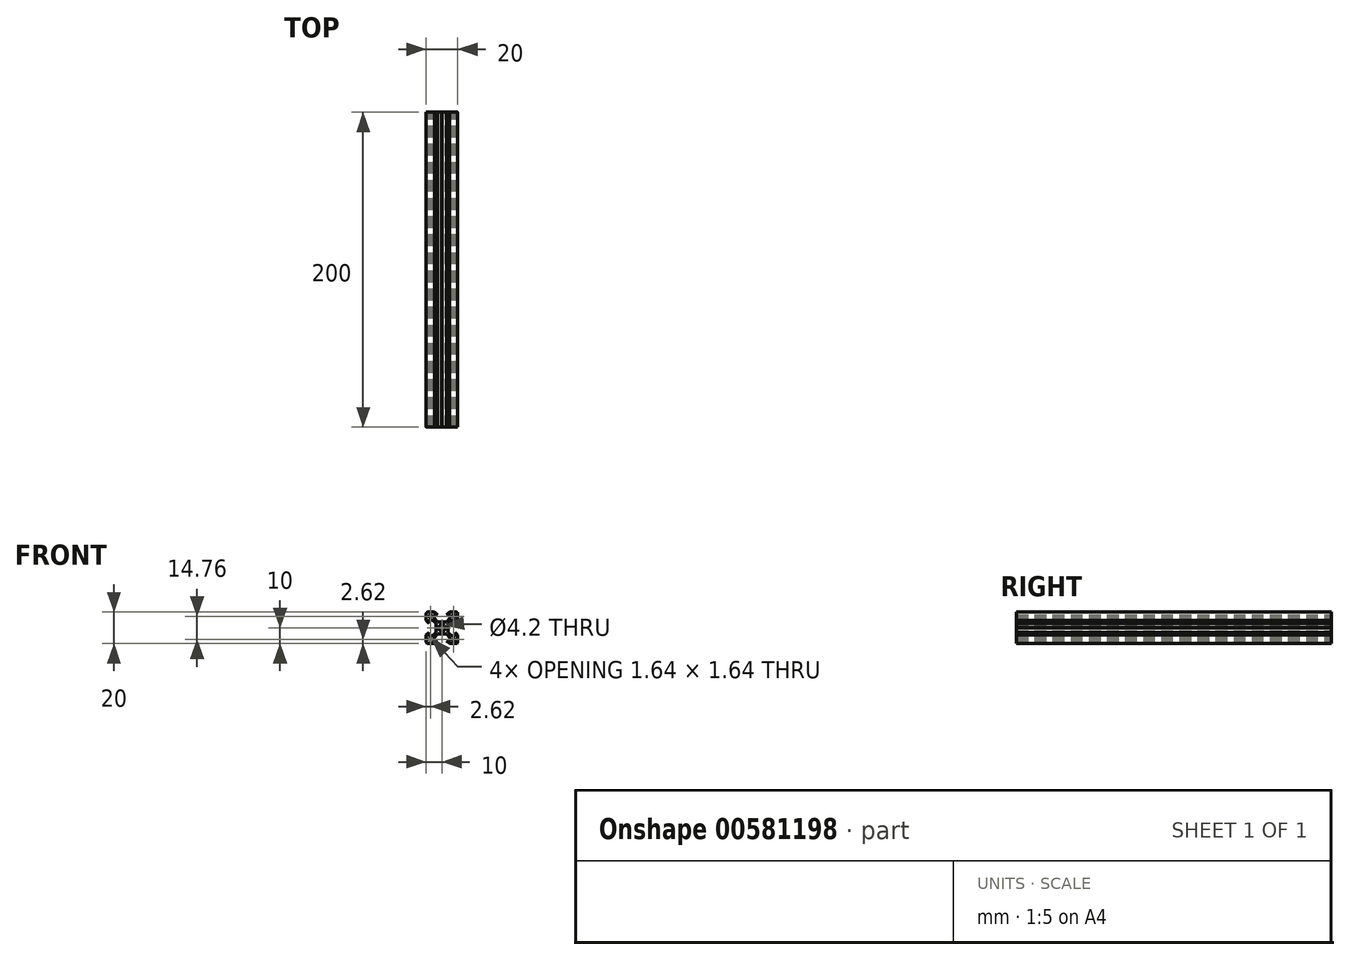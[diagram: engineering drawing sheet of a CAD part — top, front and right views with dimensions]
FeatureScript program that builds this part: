
annotation { "Feature Type Name" : "Feature", "Feature Type Description" : "" }
export const myFeature = defineFeature(function(context is Context, id is Id, definition is map)
    precondition{}
    {
        {
            var Q0;
            Q0=qCreatedBy(makeId("Front.planeOp"),FACE);
            var sketch = newSketch(context, id + "F0", { "sketchPlane" : qUnion([Q0])});
            skLineSegment(sketch, "E0.rect.bottom", {"start": v(-9, 10) * mm, "end": v(9, 10) * mm});
            skLineSegment(sketch, "E0.rect.top", {"start": v(-9, -10) * mm, "end": v(9, -10) * mm});
            skLineSegment(sketch, "E0.rect.left", {"start": v(-10, 9) * mm, "end": v(-10, -9) * mm});
            skLineSegment(sketch, "E0.rect.right", {"start": v(10, 9) * mm, "end": v(10, -9) * mm});
            skPoint(sketch, "E0.rect.middle", {"position": v(0, 0) * mm});
            skCircle(sketch, "E1", {"center": v(0, 0) * mm, "radius": 2.1 * mm});
            skPoint(sketch, "E2.visualSharp", {"position": v(-10, 10) * mm});
            skArc(sketch, "E2.filletArc", {"start": v(-9, 10) * mm, "mid": v(-9.7, 9.7) * mm, "end": v(-10, 9) * mm});
            skPoint(sketch, "E3.visualSharp", {"position": v(10, 10) * mm});
            skArc(sketch, "E3.filletArc", {"start": v(10, 9) * mm, "mid": v(9.7, 9.7) * mm, "end": v(9, 10) * mm});
            skPoint(sketch, "E4.visualSharp", {"position": v(10, -10) * mm});
            skArc(sketch, "E4.filletArc", {"start": v(9, -10) * mm, "mid": v(9.7, -9.7) * mm, "end": v(10, -9) * mm});
            skPoint(sketch, "E5.visualSharp", {"position": v(-10, -10) * mm});
            skArc(sketch, "E5.filletArc", {"start": v(-10, -9) * mm, "mid": v(-9.7, -9.7) * mm, "end": v(-9, -10) * mm});
            skLineSegment(sketch, "E6", {"start": v(10, 10) * mm, "end": v(-10, -10) * mm, "construction": true});
            skLineSegment(sketch, "E7", {"start": v(-10, 10) * mm, "end": v(10, -10) * mm, "construction": true});
            skLineSegment(sketch, "E8", {"start": v(-4.64, 10) * mm, "end": v(-2.84, 8.2) * mm});
            skLineSegment(sketch, "E9", {"start": v(-2.84, 8.2) * mm, "end": v(-5.5, 8.2) * mm});
            skLineSegment(sketch, "E10", {"start": v(-5.5, 8.2) * mm, "end": v(-5.5, 6.56) * mm});
            skLineSegment(sketch, "E11", {"start": v(-5.5, 6.56) * mm, "end": v(-2.84, 3.9) * mm});
            skLineSegment(sketch, "E12.MirrorCS", {"start": v(4.64, 10) * mm, "end": v(2.84, 8.2) * mm});
            skLineSegment(sketch, "E13.MirrorCS", {"start": v(2.84, 8.2) * mm, "end": v(5.5, 8.2) * mm});
            skLineSegment(sketch, "E14.MirrorCS", {"start": v(5.5, 8.2) * mm, "end": v(5.5, 6.56) * mm});
            skLineSegment(sketch, "E15.MirrorCS", {"start": v(5.5, 6.56) * mm, "end": v(2.84, 3.9) * mm});
            skLineSegment(sketch, "E16", {"start": v(-2.84, 3.9) * mm, "end": v(2.84, 3.9) * mm});
            skLineSegment(sketch, "E17.MirrorCS", {"start": v(-4.64, -10) * mm, "end": v(-2.84, -8.2) * mm});
            skLineSegment(sketch, "E18.MirrorCS", {"start": v(-2.84, -8.2) * mm, "end": v(-5.5, -8.2) * mm});
            skLineSegment(sketch, "E19.MirrorCS", {"start": v(-5.5, -8.2) * mm, "end": v(-5.5, -6.56) * mm});
            skLineSegment(sketch, "E20.MirrorCS", {"start": v(-5.5, -6.56) * mm, "end": v(-2.84, -3.9) * mm});
            skLineSegment(sketch, "E21.MirrorCS", {"start": v(-2.84, -3.9) * mm, "end": v(2.84, -3.9) * mm});
            skLineSegment(sketch, "E22.MirrorCS", {"start": v(5.5, -6.56) * mm, "end": v(2.84, -3.9) * mm});
            skLineSegment(sketch, "E23.MirrorCS", {"start": v(5.5, -8.2) * mm, "end": v(5.5, -6.56) * mm});
            skLineSegment(sketch, "E24.MirrorCS", {"start": v(2.84, -8.2) * mm, "end": v(5.5, -8.2) * mm});
            skLineSegment(sketch, "E25.MirrorCS", {"start": v(4.64, -10) * mm, "end": v(2.84, -8.2) * mm});
            skLineSegment(sketch, "E26.MirrorCS", {"start": v(10, -4.64) * mm, "end": v(8.2, -2.84) * mm});
            skLineSegment(sketch, "E27.MirrorCS", {"start": v(8.2, -2.84) * mm, "end": v(8.2, -5.5) * mm});
            skLineSegment(sketch, "E28.MirrorCS", {"start": v(8.2, -5.5) * mm, "end": v(6.56, -5.5) * mm});
            skLineSegment(sketch, "E29.MirrorCS", {"start": v(6.56, -5.5) * mm, "end": v(3.9, -2.84) * mm});
            skLineSegment(sketch, "E30.MirrorCS", {"start": v(3.9, -2.84) * mm, "end": v(3.9, 2.84) * mm});
            skLineSegment(sketch, "E31.MirrorCS", {"start": v(6.56, 5.5) * mm, "end": v(3.9, 2.84) * mm});
            skLineSegment(sketch, "E32.MirrorCS", {"start": v(8.2, 5.5) * mm, "end": v(6.56, 5.5) * mm});
            skLineSegment(sketch, "E33.MirrorCS", {"start": v(8.2, 2.84) * mm, "end": v(8.2, 5.5) * mm});
            skLineSegment(sketch, "E34.MirrorCS", {"start": v(10, 4.64) * mm, "end": v(8.2, 2.84) * mm});
            skLineSegment(sketch, "E35.MirrorCS", {"start": v(-8.2, 2.84) * mm, "end": v(-8.2, 5.5) * mm});
            skLineSegment(sketch, "E36.MirrorCS", {"start": v(-10, 4.64) * mm, "end": v(-8.2, 2.84) * mm});
            skLineSegment(sketch, "E37.MirrorCS", {"start": v(-8.2, 5.5) * mm, "end": v(-6.56, 5.5) * mm});
            skLineSegment(sketch, "E38.MirrorCS", {"start": v(-6.56, 5.5) * mm, "end": v(-3.9, 2.84) * mm});
            skLineSegment(sketch, "E39.MirrorCS", {"start": v(-3.9, 2.84) * mm, "end": v(-3.9, -2.84) * mm});
            skLineSegment(sketch, "E40.MirrorCS", {"start": v(-6.56, -5.5) * mm, "end": v(-3.9, -2.84) * mm});
            skLineSegment(sketch, "E41.MirrorCS", {"start": v(-8.2, -5.5) * mm, "end": v(-6.56, -5.5) * mm});
            skLineSegment(sketch, "E42.MirrorCS", {"start": v(-8.2, -2.84) * mm, "end": v(-8.2, -5.5) * mm});
            skLineSegment(sketch, "E43.MirrorCS", {"start": v(-10, -4.64) * mm, "end": v(-8.2, -2.84) * mm});
            skLineSegment(sketch, "E44", {"start": v(-8.05, 8.2) * mm, "end": v(-6.71, 8.2) * mm});
            skLineSegment(sketch, "E45", {"start": v(-6.56, 8.05) * mm, "end": v(-6.56, 8.05) * mm});
            skLineSegment(sketch, "E46", {"start": v(-6.6, 7.94) * mm, "end": v(-7.94, 6.6) * mm});
            skLineSegment(sketch, "E47", {"start": v(-8.05, 6.56) * mm, "end": v(-8.05, 6.56) * mm});
            skLineSegment(sketch, "E48", {"start": v(-8.2, 6.7) * mm, "end": v(-8.2, 8.05) * mm});
            skLineSegment(sketch, "E49.MirrorCS", {"start": v(8.2, 6.71) * mm, "end": v(8.2, 8.05) * mm});
            skLineSegment(sketch, "E50.MirrorCS", {"start": v(7.99, 6.56) * mm, "end": v(8.05, 6.56) * mm});
            skLineSegment(sketch, "E51.MirrorCS", {"start": v(6.56, 7.99) * mm, "end": v(7.99, 6.56) * mm});
            skLineSegment(sketch, "E52.MirrorCS", {"start": v(6.56, 8.05) * mm, "end": v(6.56, 7.99) * mm});
            skLineSegment(sketch, "E53.MirrorCS", {"start": v(8.05, 8.2) * mm, "end": v(6.7, 8.2) * mm});
            skLineSegment(sketch, "E54.MirrorCS", {"start": v(-8.2, -6.7) * mm, "end": v(-8.2, -8.2) * mm});
            skLineSegment(sketch, "E55.MirrorCS", {"start": v(-7.99, -6.56) * mm, "end": v(-8.05, -6.56) * mm});
            skLineSegment(sketch, "E56.MirrorCS", {"start": v(-6.6, -7.94) * mm, "end": v(-7.99, -6.56) * mm});
            skLineSegment(sketch, "E57.MirrorCS", {"start": v(-6.56, -8.05) * mm, "end": v(-6.56, -8.05) * mm});
            skLineSegment(sketch, "E58.MirrorCS", {"start": v(-8.2, -8.2) * mm, "end": v(-6.7, -8.2) * mm});
            skLineSegment(sketch, "E59.MirrorCS", {"start": v(6.56, -8.05) * mm, "end": v(6.56, -7.99) * mm});
            skLineSegment(sketch, "E60.MirrorCS", {"start": v(6.56, -7.99) * mm, "end": v(7.94, -6.6) * mm});
            skLineSegment(sketch, "E61.MirrorCS", {"start": v(8.05, -6.56) * mm, "end": v(8.2, -6.56) * mm});
            skLineSegment(sketch, "E62.MirrorCS", {"start": v(8.2, -6.56) * mm, "end": v(8.2, -8.05) * mm});
            skLineSegment(sketch, "E63.MirrorCS", {"start": v(8.05, -8.2) * mm, "end": v(6.7, -8.2) * mm});
            skLineSegment(sketch, "E64", {"start": v(-0.15, 3.9) * mm, "end": v(0, 3.75) * mm});
            skLineSegment(sketch, "E65", {"start": v(0, 3.75) * mm, "end": v(0.15, 3.9) * mm});
            skLineSegment(sketch, "E66.MirrorCS", {"start": v(-0.15, -3.9) * mm, "end": v(0, -3.75) * mm});
            skLineSegment(sketch, "E67.MirrorCS", {"start": v(0, -3.75) * mm, "end": v(0.15, -3.9) * mm});
            skLineSegment(sketch, "E68.MirrorCS", {"start": v(3.9, -0.15) * mm, "end": v(3.75, 0) * mm});
            skLineSegment(sketch, "E69.MirrorCS", {"start": v(3.75, 0) * mm, "end": v(3.9, 0.15) * mm});
            skLineSegment(sketch, "E70.MirrorCS", {"start": v(-3.9, 0.15) * mm, "end": v(-3.75, 0) * mm});
            skLineSegment(sketch, "E71.MirrorCS", {"start": v(-3.75, 0) * mm, "end": v(-3.9, -0.15) * mm});
            skPoint(sketch, "E72.visualSharp", {"position": v(-8.2, 8.2) * mm});
            skArc(sketch, "E72.filletArc", {"start": v(-8.05, 8.2) * mm, "mid": v(-8.16, 8.16) * mm, "end": v(-8.2, 8.05) * mm});
            skPoint(sketch, "E73.visualSharp", {"position": v(-6.56, 7.99) * mm});
            skArc(sketch, "E73.filletArc", {"start": v(-6.6, 7.94) * mm, "mid": v(-6.57, 8) * mm, "end": v(-6.56, 8.05) * mm});
            skPoint(sketch, "E74.visualSharp", {"position": v(-7.99, 6.56) * mm});
            skArc(sketch, "E74.filletArc", {"start": v(-8.05, 6.56) * mm, "mid": v(-8, 6.57) * mm, "end": v(-7.94, 6.6) * mm});
            skPoint(sketch, "E75.visualSharp", {"position": v(-6.56, 8.2) * mm});
            skArc(sketch, "E75.filletArc", {"start": v(-6.56, 8.05) * mm, "mid": v(-6.6, 8.16) * mm, "end": v(-6.71, 8.2) * mm});
            skPoint(sketch, "E76.visualSharp", {"position": v(-8.2, 6.56) * mm});
            skArc(sketch, "E76.filletArc", {"start": v(-8.2, 6.7) * mm, "mid": v(-8.16, 6.6) * mm, "end": v(-8.05, 6.56) * mm});
            skPoint(sketch, "E77.visualSharp", {"position": v(6.56, 8.2) * mm});
            skArc(sketch, "E77.filletArc", {"start": v(6.7, 8.2) * mm, "mid": v(6.6, 8.16) * mm, "end": v(6.56, 8.05) * mm});
            skPoint(sketch, "E78.visualSharp", {"position": v(8.2, 8.2) * mm});
            skArc(sketch, "E78.filletArc", {"start": v(8.2, 8.05) * mm, "mid": v(8.16, 8.16) * mm, "end": v(8.05, 8.2) * mm});
            skPoint(sketch, "E79.visualSharp", {"position": v(8.2, 6.56) * mm});
            skArc(sketch, "E79.filletArc", {"start": v(8.05, 6.56) * mm, "mid": v(8.16, 6.6) * mm, "end": v(8.2, 6.71) * mm});
            skPoint(sketch, "E80.visualSharp", {"position": v(6.56, -8.2) * mm});
            skArc(sketch, "E80.filletArc", {"start": v(6.56, -8.05) * mm, "mid": v(6.6, -8.16) * mm, "end": v(6.7, -8.2) * mm});
            skPoint(sketch, "E81.visualSharp", {"position": v(7.99, -6.56) * mm});
            skArc(sketch, "E81.filletArc", {"start": v(8.05, -6.56) * mm, "mid": v(8, -6.57) * mm, "end": v(7.94, -6.6) * mm});
            skPoint(sketch, "E82.visualSharp", {"position": v(8.2, -8.2) * mm});
            skArc(sketch, "E82.filletArc", {"start": v(8.05, -8.2) * mm, "mid": v(8.16, -8.16) * mm, "end": v(8.2, -8.05) * mm});
            skPoint(sketch, "E83.visualSharp", {"position": v(-6.56, -8.2) * mm});
            skArc(sketch, "E83.filletArc", {"start": v(-6.7, -8.2) * mm, "mid": v(-6.6, -8.16) * mm, "end": v(-6.56, -8.05) * mm});
            skPoint(sketch, "E84.visualSharp", {"position": v(-8.2, -6.56) * mm});
            skArc(sketch, "E84.filletArc", {"start": v(-8.05, -6.56) * mm, "mid": v(-8.16, -6.6) * mm, "end": v(-8.2, -6.7) * mm});
            skPoint(sketch, "E85.visualSharp", {"position": v(-6.56, -7.99) * mm});
            skArc(sketch, "E85.filletArc", {"start": v(-6.56, -8.05) * mm, "mid": v(-6.57, -8) * mm, "end": v(-6.6, -7.94) * mm});
            skSolve(sketch);
        }
        {
            var Q0;
            Q0=makeQuery(id+"F0.imprint","IMPRINT",FACE,{"disambiguationData":[TD([[makeQuery(id+"F0.imprint","IMPRINT",EDGE,{"derivedFrom":sQuery(id+"F0.wireOp",EDGE,"E1")}),-1.0]])]});
            extrude(context, id + "F1", {"entities" : qUnion([Q0]), "depth" : 200 * mm});
        }
    });
